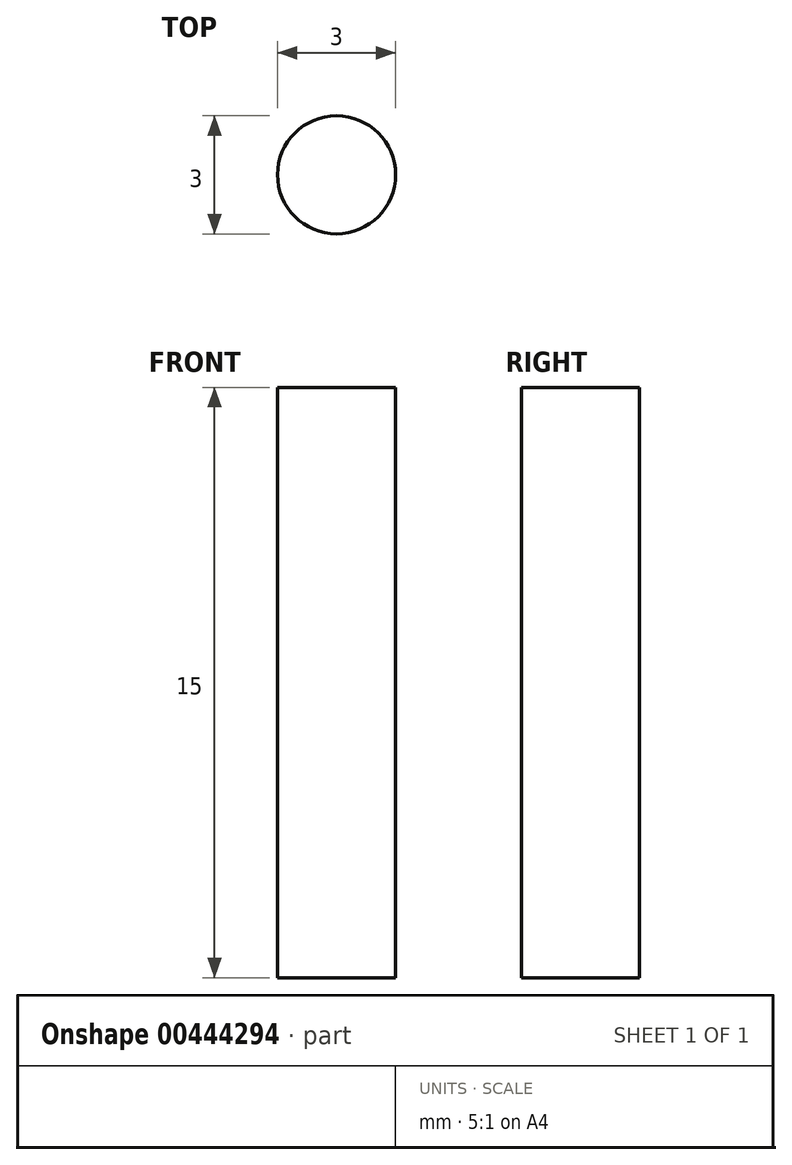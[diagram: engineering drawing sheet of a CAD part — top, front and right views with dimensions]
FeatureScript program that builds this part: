
annotation { "Feature Type Name" : "Feature", "Feature Type Description" : "" }
export const myFeature = defineFeature(function(context is Context, id is Id, definition is map)
    precondition{}
    {
        {
            var Q0;
            Q0=qCreatedBy(makeId("Top.planeOp"),FACE);
            var sketch = newSketch(context, id + "F0", { "sketchPlane" : qUnion([Q0])});
            skCircle(sketch, "E0", {"center": v(0, 0) * mm, "radius": 1.5 * mm});
            skSolve(sketch);
        }
        {
            var Q0;
            Q0 = qSketchRegion(id + "F0", true);
            extrude(context, id + "F1", {"entities" : qUnion([Q0]), "depth" : 15 * mm});
        }
    });
